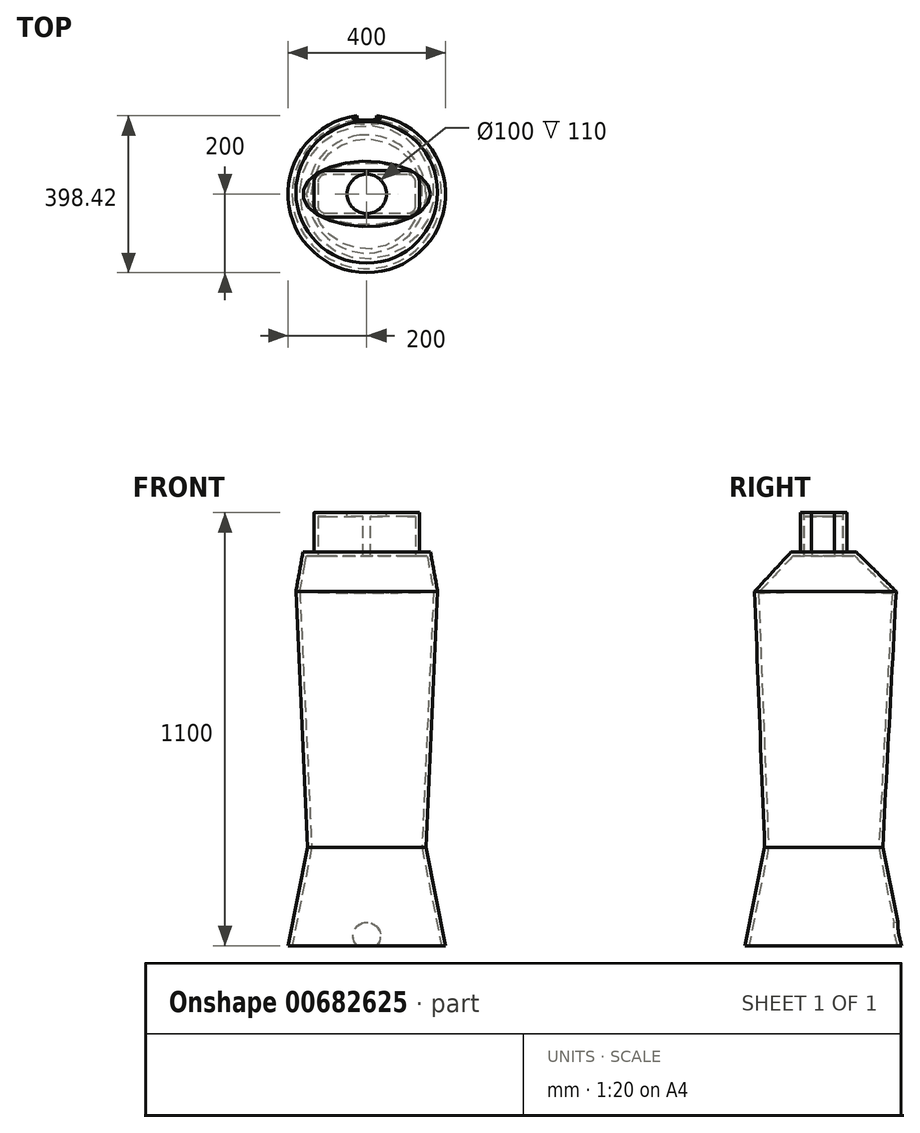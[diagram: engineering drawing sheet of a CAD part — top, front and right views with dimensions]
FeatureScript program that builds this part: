
annotation { "Feature Type Name" : "Feature", "Feature Type Description" : "" }
export const myFeature = defineFeature(function(context is Context, id is Id, definition is map)
    precondition{}
    {
        {
            var Q0;
            Q0=qCreatedBy(makeId("Top.planeOp"),FACE);
            var sketch = newSketch(context, id + "F0", { "sketchPlane" : qUnion([Q0])});
            skPoint(sketch, "E0", {"position": v(0, 0) * mm});
            skEllipse(sketch, "E1", {"center": v(0, 0) * mm, "majorRadius": 162 * mm, "minorRadius": 83.05 * mm, "majorAxis": v(1, 0)});
            skSolve(sketch);
        }
        {
            var Q0;
            Q0=qCreatedBy(makeId("Top.planeOp"),FACE);
            cPlane(context, id + "F1", {"entities" : qUnion([Q0]), "cplaneType" : CPlaneType.OFFSET, "offset" : 100 * mm, "oppositeDirection" : true, "width" : 150 * mm, "height" : 150 * mm});
        }
        {
            var Q0;
            Q0=qCreatedBy(makeId("Top.planeOp"),FACE);
            cPlane(context, id + "F2", {"entities" : qUnion([Q0]), "cplaneType" : CPlaneType.OFFSET, "offset" : 750 * mm, "oppositeDirection" : true, "width" : 150 * mm, "height" : 150 * mm});
        }
        {
            var Q0;
            Q0=qCreatedBy(makeId("Top.planeOp"),FACE);
            cPlane(context, id + "F3", {"entities" : qUnion([Q0]), "cplaneType" : CPlaneType.OFFSET, "offset" : 1000 * mm, "oppositeDirection" : true, "width" : 150 * mm, "height" : 150 * mm});
        }
        {
            var Q0;
            Q0=qCreatedBy(id+"F1.planeOp",FACE);
            var sketch = newSketch(context, id + "F4", { "sketchPlane" : qUnion([Q0])});
            skCircle(sketch, "E2", {"center": v(0, 4.36) * mm, "radius": 180 * mm});
            skSolve(sketch);
        }
        {
            var Q0;
            Q0=makeQuery(id+"F0.imprint","IMPRINT",FACE,{"disambiguationData":[TD([[makeQuery(id+"F0.imprint","IMPRINT",EDGE,{"derivedFrom":sQuery(id+"F0.wireOp",EDGE,"E1")}),1.0]])]});
            var Q1;
            Q1=makeQuery(id+"F4.imprint","IMPRINT",FACE,{"disambiguationData":[TD([[makeQuery(id+"F4.imprint","IMPRINT",EDGE,{"derivedFrom":sQuery(id+"F4.wireOp",EDGE,"E2")}),1.0]])]});
            loft(context, id + "F5", {"sheetProfilesArray" : [{ "sheetProfileEntities" : qUnion([Q0]) }, { "sheetProfileEntities" : qUnion([Q1]) }]});
        }
        {
            var Q0;
            Q0=qCreatedBy(id+"F2.planeOp",FACE);
            var sketch = newSketch(context, id + "F6", { "sketchPlane" : qUnion([Q0])});
            skCircle(sketch, "E3", {"center": v(0, 0) * mm, "radius": 150 * mm});
            skSolve(sketch);
        }
        {
            var Q1;
            Q1=makeQuery(id+"F5.opLoft","CAP_FACE",FACE,{"disambiguationData":[OSD([makeQuery(id+"F4.imprint","IMPRINT",FACE,{"disambiguationData":[TD([[makeQuery(id+"F4.imprint","IMPRINT",EDGE,{"derivedFrom":sQuery(id+"F4.wireOp",EDGE,"E2")}),1.0]])]})])],"isStart":true});
            var Q2;
            Q2=makeQuery(id+"F6.imprint","IMPRINT",FACE,{"disambiguationData":[TD([[makeQuery(id+"F6.imprint","IMPRINT",EDGE,{"derivedFrom":sQuery(id+"F6.wireOp",EDGE,"E3")}),1.0]])]});
            loft(context, id + "F7", {"operationType" : NewBodyOperationType.ADD, "sheetProfilesArray" : [{ "sheetProfileEntities" : qUnion([Q1]) }, { "sheetProfileEntities" : qUnion([Q2]) }]});
        }
        {
            var Q0;
            Q0=qCreatedBy(id+"F3.planeOp",FACE);
            var sketch = newSketch(context, id + "F8", { "sketchPlane" : qUnion([Q0])});
            skCircle(sketch, "E4", {"center": v(0, 0) * mm, "radius": 200 * mm});
            skSolve(sketch);
        }
        {
            var Q1;
            Q1=makeQuery(id+"F7.opLoft","CAP_FACE",FACE,{"disambiguationData":[OSD([makeQuery(id+"F6.imprint","IMPRINT",FACE,{"disambiguationData":[TD([[makeQuery(id+"F6.imprint","IMPRINT",EDGE,{"derivedFrom":sQuery(id+"F6.wireOp",EDGE,"E3")}),1.0]])]})])],"isStart":true});
            var Q2;
            Q2=makeQuery(id+"F8.imprint","IMPRINT",FACE,{"disambiguationData":[TD([[makeQuery(id+"F8.imprint","IMPRINT",EDGE,{"derivedFrom":sQuery(id+"F8.wireOp",EDGE,"E4")}),1.0]])]});
            loft(context, id + "F9", {"operationType" : NewBodyOperationType.ADD, "sheetProfilesArray" : [{ "sheetProfileEntities" : qUnion([Q1]) }, { "sheetProfileEntities" : qUnion([Q2]) }]});
        }
        {
            var Q0;
            Q0=makeQuery(id+"F5.opLoft","CAP_FACE",FACE,{"disambiguationData":[OSD([makeQuery(id+"F0.imprint","IMPRINT",FACE,{"disambiguationData":[TD([[makeQuery(id+"F0.imprint","IMPRINT",EDGE,{"derivedFrom":sQuery(id+"F0.wireOp",EDGE,"E1")}),1.0]])]})])],"isStart":true});
            var sketch = newSketch(context, id + "F10", { "sketchPlane" : qUnion([Q0])});
            skArc(sketch, "E5.0.0", {"start": v(-162, -30.54) * mm, "mid": v(-151.45, -62.37) * mm, "end": v(-125.05, -83.05) * mm});
            skLineSegment(sketch, "E5.0.1", {"start": v(-125.05, -83.05) * mm, "end": v(125.05, -83.05) * mm});
            skArc(sketch, "E5.0.2", {"start": v(125.05, -83.05) * mm, "mid": v(151.45, -62.37) * mm, "end": v(162, -30.54) * mm});
            skLineSegment(sketch, "E5.0.3", {"start": v(162, -30.54) * mm, "end": v(162, 27.46) * mm});
            skArc(sketch, "E5.0.4", {"start": v(162, 27.46) * mm, "mid": v(152.32, 61.1) * mm, "end": v(125.05, 83.05) * mm});
            skLineSegment(sketch, "E5.0.5", {"start": v(125.05, 83.05) * mm, "end": v(-125.05, 83.05) * mm});
            skArc(sketch, "E5.0.6", {"start": v(-125.05, 83.05) * mm, "mid": v(-152.32, 61.1) * mm, "end": v(-162, 27.46) * mm});
            skLineSegment(sketch, "E5.0.7", {"start": v(-162, 27.46) * mm, "end": v(-162, -30.54) * mm});
            skArc(sketch, "E6.0.0", {"start": v(-134, -30.54) * mm, "mid": v(-124.69, -50.76) * mm, "end": v(-104, -59) * mm});
            skLineSegment(sketch, "E6.0.1", {"start": v(-104, -59) * mm, "end": v(104, -59) * mm});
            skArc(sketch, "E6.0.2", {"start": v(104, -59) * mm, "mid": v(124.69, -50.76) * mm, "end": v(134, -30.54) * mm});
            skLineSegment(sketch, "E6.0.3", {"start": v(134, -30.54) * mm, "end": v(134, 27.46) * mm});
            skArc(sketch, "E6.0.4", {"start": v(134, 27.46) * mm, "mid": v(125.78, 49.68) * mm, "end": v(104, 59) * mm});
            skLineSegment(sketch, "E6.0.5", {"start": v(104, 59) * mm, "end": v(-104, 59) * mm});
            skArc(sketch, "E6.0.6", {"start": v(-104, 59) * mm, "mid": v(-125.78, 49.68) * mm, "end": v(-134, 27.46) * mm});
            skLineSegment(sketch, "E6.0.7", {"start": v(-134, 27.46) * mm, "end": v(-134, -30.54) * mm});
            skSolve(sketch);
        }
        {
            var Q0;
            {var subQ1=makeQuery(id+"F5.opLoft","MID_CAP_EDGE",EDGE,{"disambiguationData":[OSD([sQuery(id+"F0.wireOp",EDGE,"E1")])],"capPos":0.0});var subQ8=sQuery(id+"F10.wireOp",EDGE,"E6.0.1");var subQ9=makeQuery(id+"F10.imprint","INTERSECT",VERTEX,{"disambiguationData":[OD(0.0)],"derivedFrom":[subQ1,subQ8]});Q0=makeQuery(id+"F10.imprint","IMPRINT",FACE,{"disambiguationData":[TD([[makeQuery(id+"F10.imprint","IMPRINT",EDGE,{"disambiguationData":[TD([[subQ9,-1.0]])],"derivedFrom":subQ8}),1.0]])]});}
            var Q1;
            {var subQ0=sQuery(id+"F10.wireOp",EDGE,"E6.0.6");var subQ1=sQuery(id+"F10.wireOp",EDGE,"E6.0.5");var subQ2=makeQuery(id+"F10.imprint","INTERSECT",VERTEX,{"derivedFrom":[subQ1,subQ0]});Q1=makeQuery(id+"F10.imprint","IMPRINT",FACE,{"disambiguationData":[TD([[makeQuery(id+"F10.imprint","IMPRINT",EDGE,{"disambiguationData":[TD([[subQ2,1.0]])],"derivedFrom":subQ1}),1.0]])]});}
            var Q2;
            {var subQ0=sQuery(id+"F10.wireOp",EDGE,"E6.0.0");Q2=makeQuery(id+"F10.imprint","IMPRINT",FACE,{"disambiguationData":[TD([[makeQuery(id+"F10.imprint","IMPRINT",EDGE,{"derivedFrom":subQ0}),1.0]])]});}
            var Q3;
            {var subQ0=sQuery(id+"F10.wireOp",EDGE,"E6.0.5");var subQ1=sQuery(id+"F10.wireOp",EDGE,"E6.0.4");var subQ2=makeQuery(id+"F10.imprint","INTERSECT",VERTEX,{"derivedFrom":[subQ1,subQ0]});Q3=makeQuery(id+"F10.imprint","IMPRINT",FACE,{"disambiguationData":[TD([[makeQuery(id+"F10.imprint","IMPRINT",EDGE,{"disambiguationData":[TD([[subQ2,1.0]])],"derivedFrom":subQ1}),1.0]])]});}
            var Q4;
            {var subQ0=sQuery(id+"F10.wireOp",EDGE,"E6.0.2");Q4=makeQuery(id+"F10.imprint","IMPRINT",FACE,{"disambiguationData":[TD([[makeQuery(id+"F10.imprint","IMPRINT",EDGE,{"derivedFrom":subQ0}),1.0]])]});}
            extrude(context, id + "F11", {"entities" : qUnion([Q0, Q1, Q2, Q3, Q4]), "operationType" : NewBodyOperationType.ADD, "depth" : 100 * mm, "offsetDistance" : 25 * mm});
        }
        {
            var Q0;
            Q0=makeQuery(id+"F9.opLoft","CAP_FACE",FACE,{"disambiguationData":[OSD([makeQuery(id+"F8.imprint","IMPRINT",FACE,{"disambiguationData":[TD([[makeQuery(id+"F8.imprint","IMPRINT",EDGE,{"derivedFrom":sQuery(id+"F8.wireOp",EDGE,"E4")}),1.0]])]})])],"isStart":true});
            shell(context, id + "F12", {"entities" : qUnion([Q0]), "thickness" : 10 * mm});
        }
        {
            var Q0;
            Q0=makeQuery(id+"F11.opExtrude","CAP_FACE",FACE,{"disambiguationData":[OSD([sQuery(id+"F10.wireOp",EDGE,"E6.0.0"),sQuery(id+"F10.wireOp",EDGE,"E6.0.1"),sQuery(id+"F10.wireOp",EDGE,"E6.0.2"),sQuery(id+"F10.wireOp",EDGE,"E6.0.3"),sQuery(id+"F10.wireOp",EDGE,"E6.0.4"),sQuery(id+"F10.wireOp",EDGE,"E6.0.5"),sQuery(id+"F10.wireOp",EDGE,"E6.0.6"),sQuery(id+"F10.wireOp",EDGE,"E6.0.7")])],"isStart":false});
            var sketch = newSketch(context, id + "F13", { "sketchPlane" : qUnion([Q0])});
            skCircle(sketch, "E7", {"center": v(0, 0) * mm, "radius": 50 * mm});
            skSolve(sketch);
        }
        {
            var Q0;
            Q0=makeQuery(id+"F13.imprint","IMPRINT",FACE,{"disambiguationData":[TD([[makeQuery(id+"F13.imprint","IMPRINT",EDGE,{"derivedFrom":sQuery(id+"F13.wireOp",EDGE,"E7")}),1.0]])]});
            extrude(context, id + "F14", {"entities" : qUnion([Q0]), "operationType" : NewBodyOperationType.REMOVE, "endBound" : BoundingType.THROUGH_ALL, "oppositeDirection" : true, "depth" : 25 * mm, "offsetDistance" : 25 * mm});
        }
        {
            var Q0;
            Q0=qCreatedBy(makeId("Front.planeOp"),FACE);
            var sketch = newSketch(context, id + "F15", { "sketchPlane" : qUnion([Q0])});
            skLineSegment(sketch, "E8", {"start": v(-200, -1000) * mm, "end": v(-150, -750) * mm});
            skLineSegment(sketch, "E9", {"start": v(150, -750) * mm, "end": v(200, -1000) * mm});
            skCircle(sketch, "E10", {"center": v(0, -975) * mm, "radius": 25 * mm});
            skSolve(sketch);
        }
        {
            var Q0;
            Q0=makeQuery(id+"F15.imprint","IMPRINT",FACE,{"disambiguationData":[TD([[makeQuery(id+"F15.imprint","IMPRINT",EDGE,{"derivedFrom":sQuery(id+"F15.wireOp",EDGE,"E10")}),1.0]])]});
            extrude(context, id + "F16", {"entities" : qUnion([Q0]), "operationType" : NewBodyOperationType.REMOVE, "oppositeDirection" : true, "depth" : 400 * mm, "offsetDistance" : 25 * mm, "hasDraft" : true, "draftAngle" : 3 * degree});
        }
    });
